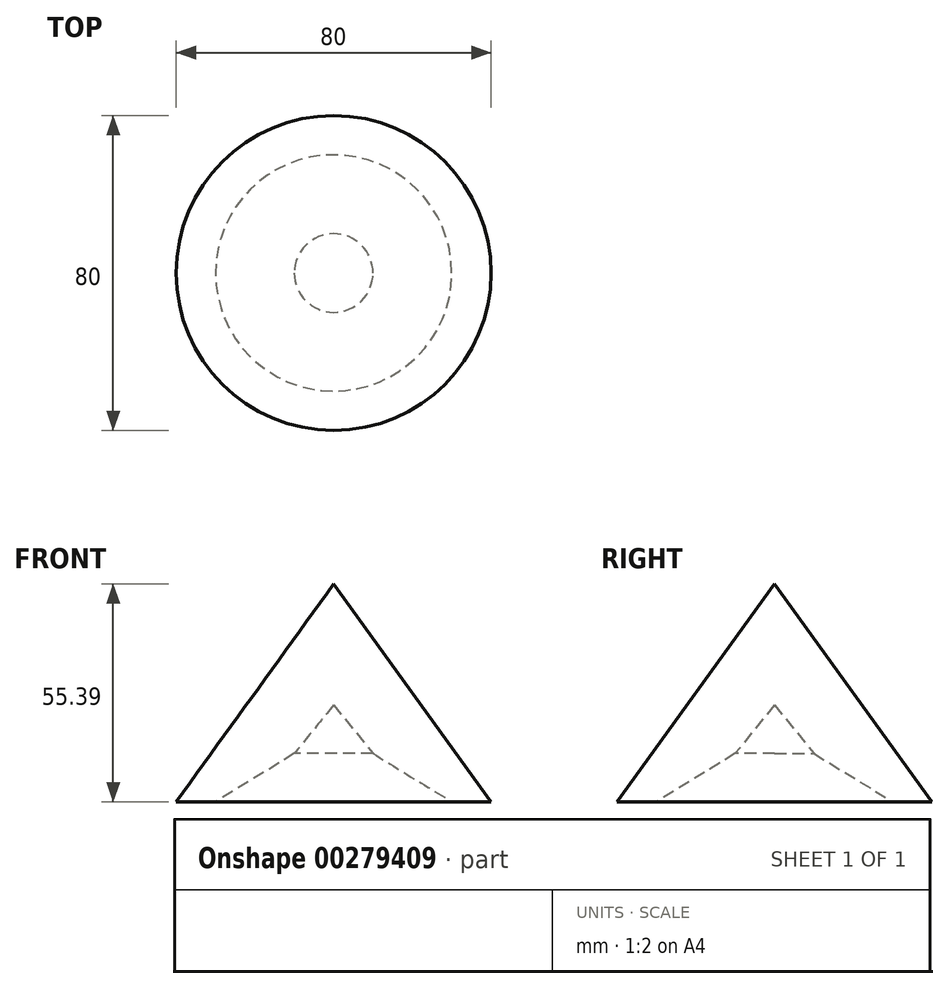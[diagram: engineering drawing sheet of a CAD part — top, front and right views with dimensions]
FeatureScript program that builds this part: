
annotation { "Feature Type Name" : "Feature", "Feature Type Description" : "" }
export const myFeature = defineFeature(function(context is Context, id is Id, definition is map)
    precondition{}
    {
        {
            var Q0;
            Q0=qCreatedBy(makeId("Front.planeOp"),FACE);
            var sketch = newSketch(context, id + "F0", { "sketchPlane" : qUnion([Q0])});
            skLineSegment(sketch, "E0", {"start": v(-45.85, 47.62) * mm, "end": v(-45.85, 16.85) * mm});
            skLineSegment(sketch, "E1", {"start": v(-15.85, -7.77) * mm, "end": v(-5.85, -7.77) * mm});
            skLineSegment(sketch, "E2", {"start": v(-5.85, -7.77) * mm, "end": v(-45.85, 47.62) * mm});
            skLineSegment(sketch, "E3", {"start": v(-45.85, 16.85) * mm, "end": v(-35.85, 4.54) * mm});
            skPoint(sketch, "E4.orphan", {"position": v(-45.85, -7.77) * mm});
            skLineSegment(sketch, "E5", {"start": v(-35.85, 4.54) * mm, "end": v(-15.85, -7.77) * mm});
            skPoint(sketch, "E6.orphan", {"position": v(-25.85, -7.77) * mm});
            skSolve(sketch);
        }
        {
            var Q0;
            Q0 = qSketchRegion(id + "F0", true);
            var Q1;
            Q1=sQuery(id+"F0.wireOp",EDGE,"E0");
            revolve(context, id + "F1", {"entities" : qUnion([Q0]), "axis" : qUnion([Q1]), "revolveType" : RevolveType.FULL});
        }
    });
